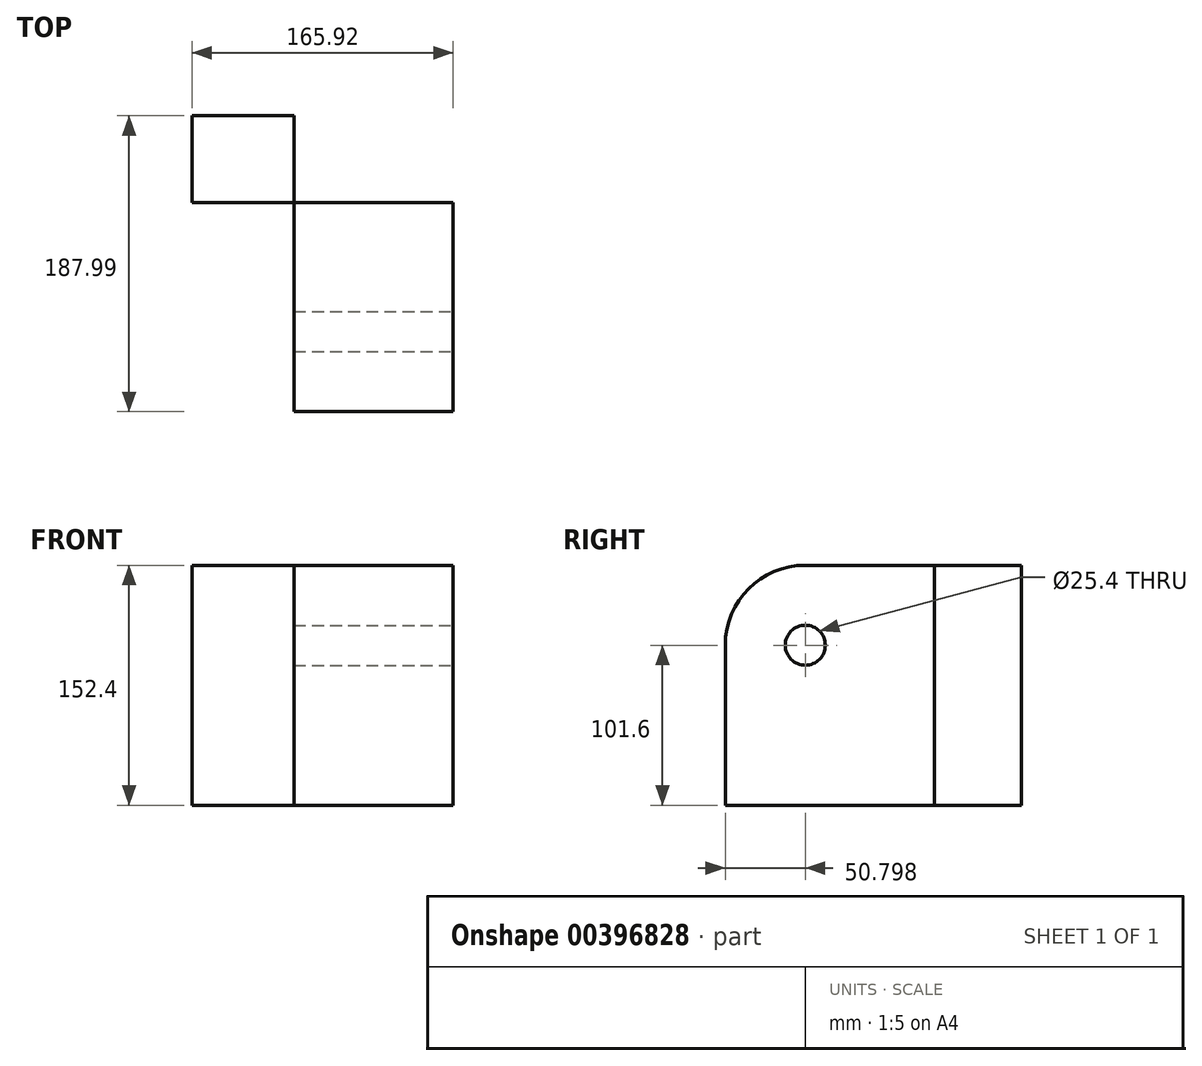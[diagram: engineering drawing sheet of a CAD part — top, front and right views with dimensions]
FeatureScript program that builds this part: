
annotation { "Feature Type Name" : "Feature", "Feature Type Description" : "" }
export const myFeature = defineFeature(function(context is Context, id is Id, definition is map)
    precondition{}
    {
        {
            var Q0;
            Q0=qCreatedBy(makeId("Top.planeOp"),FACE);
            var sketch = newSketch(context, id + "F0", { "sketchPlane" : qUnion([Q0])});
            skLineSegment(sketch, "E0.bottom", {"start": v(0, 0) * mm, "end": v(64.75, 0) * mm});
            skLineSegment(sketch, "E0.top", {"start": v(0, -55.1) * mm, "end": v(64.75, -55.1) * mm});
            skLineSegment(sketch, "E0.left", {"start": v(0, 0) * mm, "end": v(0, -55.1) * mm});
            skLineSegment(sketch, "E0.right", {"start": v(64.75, 0) * mm, "end": v(64.75, -55.1) * mm});
            skLineSegment(sketch, "E1.bottom", {"start": v(64.75, -55.1) * mm, "end": v(165.92, -55.1) * mm});
            skLineSegment(sketch, "E1.top", {"start": v(64.75, -188) * mm, "end": v(165.92, -188) * mm});
            skLineSegment(sketch, "E1.left", {"start": v(64.75, -55.1) * mm, "end": v(64.75, -188) * mm});
            skLineSegment(sketch, "E1.right", {"start": v(165.92, -55.1) * mm, "end": v(165.92, -188) * mm});
            skSolve(sketch);
        }
        {
            var Q0;
            Q0=makeQuery(id+"F0.imprint","IMPRINT",FACE,{"disambiguationData":[TD([[makeQuery(id+"F0.imprint","IMPRINT",EDGE,{"derivedFrom":sQuery(id+"F0.wireOp",EDGE,"E1.bottom")}),-1.0]])]});
            var Q1;
            Q1 = qSketchRegion(id + "F0", true);
            extrude(context, id + "F1", {"entities" : qUnion([Q0, Q1]), "depth" : 152.4 * mm});
        }
        {
            var Q0;
            Q0=makeQuery(id+"F1.opExtrude","CAP_EDGE",EDGE,{"disambiguationData":[OSD([sQuery(id+"F0.wireOp",EDGE,"E1.top")])],"isStart":false});
            fillet(context, id + "F2", {"entities" : qUnion([Q0]), "radius" : 50.8 * mm, "tangentPropagation" : true, "allowEdgeOverflow" : false});
        }
        {
            var Q0;
            Q0=makeQuery(id+"F1.opExtrude","SWEPT_FACE",FACE,{"disambiguationData":[OSD([sQuery(id+"F0.wireOp",EDGE,"E1.right")])]});
            var sketch = newSketch(context, id + "F3", { "sketchPlane" : qUnion([Q0])});
            skPoint(sketch, "E2", {"position": v(-137.2, 101.6) * mm});
            skSolve(sketch);
        }
        {
            var Q0;
            Q0=sQuery(id+"F3.wireOp",VERTEX,"E2");
            var Q1;
            Q1=makeQuery(id+"F1.opExtrude","SWEPT_BODY",BODY,{"disambiguationData":[OSD([sQuery(id+"F0.wireOp",EDGE,"E1.bottom"),sQuery(id+"F0.wireOp",EDGE,"E1.top"),sQuery(id+"F0.wireOp",EDGE,"E1.left"),sQuery(id+"F0.wireOp",EDGE,"E1.right")])]});
            hole(context, id + "F4", {"style" : HoleStyle.SIMPLE, "endStyle" : HoleEndStyle.THROUGH, "holeDiameter" : 25.4 * mm, "isTappedThrough" : true, "tappedDepth" : 12.7 * mm, "tapClearance" : 3, "locations" : qUnion([Q0]), "scope" : qUnion([Q1])});
        }
    });
